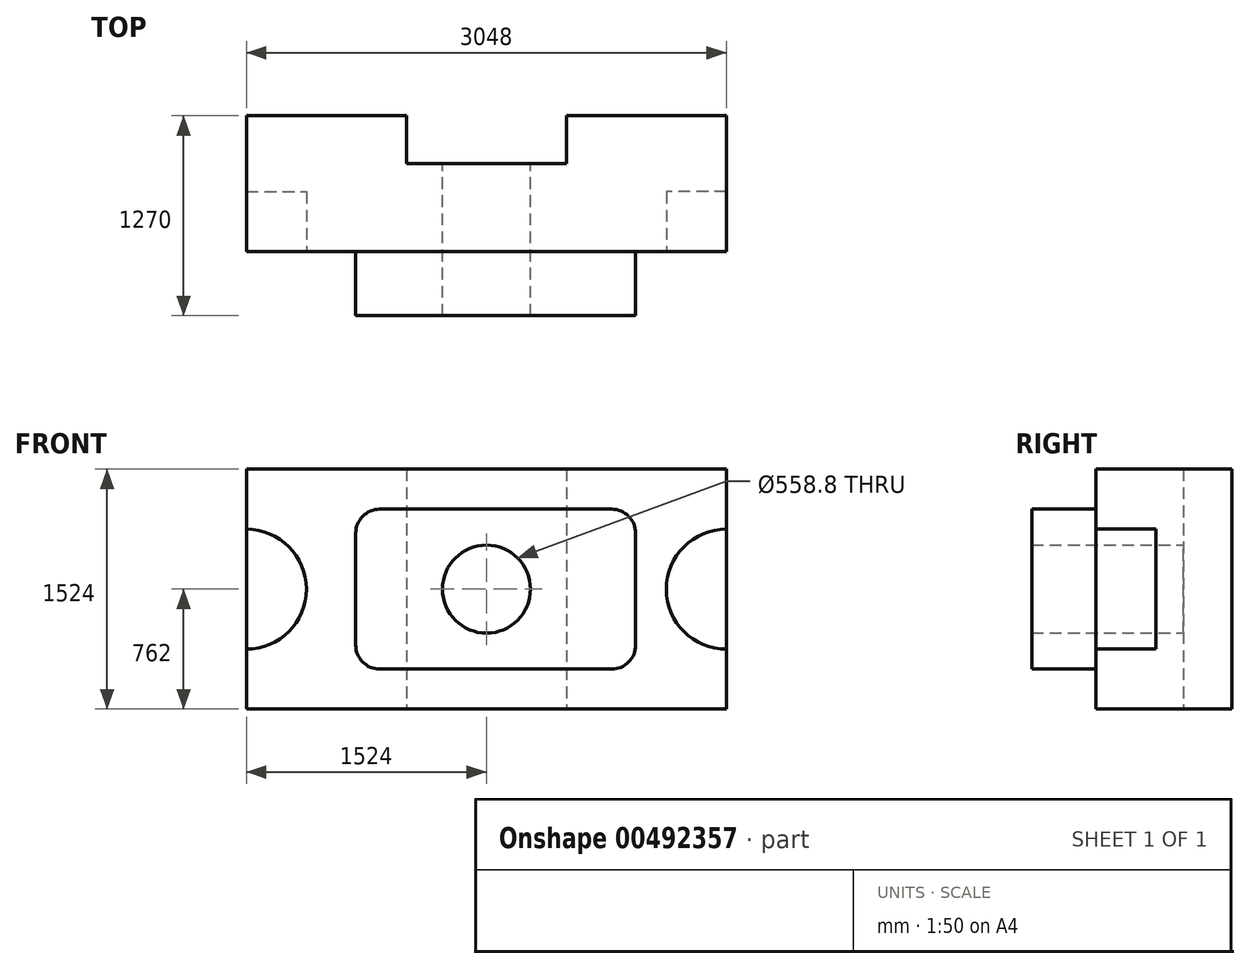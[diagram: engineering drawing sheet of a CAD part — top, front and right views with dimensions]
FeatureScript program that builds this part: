
annotation { "Feature Type Name" : "Feature", "Feature Type Description" : "" }
export const myFeature = defineFeature(function(context is Context, id is Id, definition is map)
    precondition{}
    {
        {
            var Q0;
            Q0=qCreatedBy(makeId("Front.planeOp"),FACE);
            var sketch = newSketch(context, id + "F0", { "sketchPlane" : qUnion([Q0])});
            skLineSegment(sketch, "E0.bottom", {"start": v(1524, -762) * mm, "end": v(-1524, -762) * mm});
            skLineSegment(sketch, "E0.top", {"start": v(1524, 762) * mm, "end": v(-1524, 762) * mm});
            skLineSegment(sketch, "E0.left", {"start": v(1524, -762) * mm, "end": v(1524, 762) * mm});
            skLineSegment(sketch, "E0.right", {"start": v(-1524, -762) * mm, "end": v(-1524, 762) * mm});
            skPoint(sketch, "E0.middle", {"position": v(0, 0) * mm});
            skSolve(sketch);
        }
        {
            var Q0;
            Q0=makeQuery(id+"F0.imprint","IMPRINT",FACE,{"disambiguationData":[TD([[makeQuery(id+"F0.imprint","IMPRINT",EDGE,{"derivedFrom":sQuery(id+"F0.wireOp",EDGE,"E0.bottom")}),-1.0]])]});
            extrude(context, id + "F1", {"entities" : qUnion([Q0]), "depth" : 863.6 * mm});
        }
        {
            var Q0;
            Q0=makeQuery(id+"F1.opExtrude","CAP_FACE",FACE,{"disambiguationData":[OSD([sQuery(id+"F0.wireOp",EDGE,"E0.bottom"),sQuery(id+"F0.wireOp",EDGE,"E0.top"),sQuery(id+"F0.wireOp",EDGE,"E0.left"),sQuery(id+"F0.wireOp",EDGE,"E0.right")])],"isStart":false});
            var sketch = newSketch(context, id + "F2", { "sketchPlane" : qUnion([Q0])});
            skArc(sketch, "E1", {"start": v(-1524, -381) * mm, "mid": v(-1143, 0) * mm, "end": v(-1524, 381) * mm});
            skArc(sketch, "E2", {"start": v(1524, 381) * mm, "mid": v(1143, 0) * mm, "end": v(1524, -381) * mm});
            skLineSegment(sketch, "E3", {"start": v(-1524, 381) * mm, "end": v(-1524, -381) * mm});
            skLineSegment(sketch, "E4", {"start": v(1524, 381) * mm, "end": v(1524, -381) * mm});
            skSolve(sketch);
        }
        {
            var Q0;
            Q0=makeQuery(id+"F2.imprint","IMPRINT",FACE,{"disambiguationData":[TD([[makeQuery(id+"F2.imprint","IMPRINT",EDGE,{"derivedFrom":sQuery(id+"F2.wireOp",EDGE,"E1")}),1.0]])]});
            var Q1;
            Q1=makeQuery(id+"F2.imprint","IMPRINT",FACE,{"disambiguationData":[TD([[makeQuery(id+"F2.imprint","IMPRINT",EDGE,{"derivedFrom":sQuery(id+"F2.wireOp",EDGE,"E2")}),1.0]])]});
            extrude(context, id + "F3", {"entities" : qUnion([Q0, Q1]), "operationType" : NewBodyOperationType.REMOVE, "oppositeDirection" : true, "depth" : 381 * mm});
        }
        {
            var Q0;
            Q0=makeQuery(id+"F1.opExtrude","SWEPT_FACE",FACE,{"disambiguationData":[OSD([sQuery(id+"F0.wireOp",EDGE,"E0.bottom")])]});
            var sketch = newSketch(context, id + "F4", { "sketchPlane" : qUnion([Q0])});
            skLineSegment(sketch, "E5.top", {"start": v(508, 304.8) * mm, "end": v(-508, 304.8) * mm});
            skLineSegment(sketch, "E5.left", {"start": v(508, 0) * mm, "end": v(508, 304.8) * mm});
            skLineSegment(sketch, "E5.right", {"start": v(-508, 0) * mm, "end": v(-508, 304.8) * mm});
            skPoint(sketch, "E5.middle", {"position": v(0, 0) * mm});
            skLineSegment(sketch, "E6", {"start": v(-508, 0) * mm, "end": v(508, 0) * mm});
            skPoint(sketch, "E5.bottom.end.orphan", {"position": v(-508, -304.8) * mm});
            skPoint(sketch, "E7.orphan", {"position": v(508, -304.8) * mm});
            skSolve(sketch);
        }
        {
            var Q0;
            Q0=makeQuery(id+"F4.imprint","IMPRINT",FACE,{"disambiguationData":[TD([[makeQuery(id+"F4.imprint","IMPRINT",EDGE,{"derivedFrom":sQuery(id+"F4.wireOp",EDGE,"E5.top")}),1.0]])]});
            extrude(context, id + "F5", {"entities" : qUnion([Q0]), "operationType" : NewBodyOperationType.REMOVE, "endBound" : BoundingType.THROUGH_ALL, "oppositeDirection" : true, "depth" : 25.4 * mm});
        }
        {
            var Q0;
            Q0=makeQuery(id+"F1.opExtrude","CAP_FACE",FACE,{"disambiguationData":[OSD([sQuery(id+"F0.wireOp",EDGE,"E0.bottom"),sQuery(id+"F0.wireOp",EDGE,"E0.top"),sQuery(id+"F0.wireOp",EDGE,"E0.left"),sQuery(id+"F0.wireOp",EDGE,"E0.right")])],"isStart":false});
            var sketch = newSketch(context, id + "F6", { "sketchPlane" : qUnion([Q0])});
            skLineSegment(sketch, "E8.bottom", {"start": v(795.49, 508) * mm, "end": v(-677.71, 508) * mm});
            skLineSegment(sketch, "E8.top", {"start": v(795.49, -508) * mm, "end": v(-677.71, -508) * mm});
            skLineSegment(sketch, "E8.left", {"start": v(947.89, 355.6) * mm, "end": v(947.89, -355.6) * mm});
            skLineSegment(sketch, "E8.right", {"start": v(-830.11, 355.6) * mm, "end": v(-830.11, -355.6) * mm});
            skPoint(sketch, "E8.middle", {"position": v(58.89, 0) * mm});
            skPoint(sketch, "E9.visualSharp", {"position": v(-830.11, 508) * mm});
            skArc(sketch, "E9.filletArc", {"start": v(-677.71, 508) * mm, "mid": v(-785.48, 463.36) * mm, "end": v(-830.11, 355.6) * mm});
            skPoint(sketch, "E10.visualSharp", {"position": v(947.89, 508) * mm});
            skArc(sketch, "E10.filletArc", {"start": v(947.89, 355.6) * mm, "mid": v(903.25, 463.36) * mm, "end": v(795.49, 508) * mm});
            skPoint(sketch, "E11.visualSharp", {"position": v(947.89, -508) * mm});
            skArc(sketch, "E11.filletArc", {"start": v(795.49, -508) * mm, "mid": v(903.25, -463.36) * mm, "end": v(947.89, -355.6) * mm});
            skPoint(sketch, "E12.visualSharp", {"position": v(-830.11, -508) * mm});
            skArc(sketch, "E12.filletArc", {"start": v(-830.11, -355.6) * mm, "mid": v(-785.48, -463.36) * mm, "end": v(-677.71, -508) * mm});
            skSolve(sketch);
        }
        {
            var Q0;
            Q0=makeQuery(id+"F6.imprint","IMPRINT",FACE,{"disambiguationData":[TD([[makeQuery(id+"F6.imprint","IMPRINT",EDGE,{"derivedFrom":sQuery(id+"F6.wireOp",EDGE,"E8.bottom")}),1.0]])]});
            extrude(context, id + "F7", {"entities" : qUnion([Q0]), "operationType" : NewBodyOperationType.ADD, "depth" : 406.4 * mm});
        }
        {
            var Q0;
            Q0=makeQuery(id+"F1.opExtrude","CAP_FACE",FACE,{"disambiguationData":[OSD([sQuery(id+"F0.wireOp",EDGE,"E0.bottom"),sQuery(id+"F0.wireOp",EDGE,"E0.top"),sQuery(id+"F0.wireOp",EDGE,"E0.left"),sQuery(id+"F0.wireOp",EDGE,"E0.right")])],"isStart":false});
            var sketch = newSketch(context, id + "F8", { "sketchPlane" : qUnion([Q0])});
            skCircle(sketch, "E13", {"center": v(0, 0) * mm, "radius": 279.4 * mm});
            skSolve(sketch);
        }
        {
            var Q0;
            Q0 = qSketchRegion(id + "F8", true);
            extrude(context, id + "F9", {"entities" : qUnion([Q0]), "operationType" : NewBodyOperationType.REMOVE, "endBound" : BoundingType.THROUGH_ALL, "depth" : 25.4 * mm});
        }
        {
            var Q0;
            Q0=makeQuery(id+"F9.boolean.opBoolean","COPY",FACE,{"derivedFrom":makeQuery(id+"F9.opExtrude","CAP_FACE",FACE,{"disambiguationData":[OSD([sQuery(id+"F8.wireOp",EDGE,"E13")])],"isStart":true})});
            extrude(context, id + "F10", {"entities" : qUnion([Q0]), "operationType" : NewBodyOperationType.REMOVE, "endBound" : BoundingType.THROUGH_ALL, "oppositeDirection" : true, "depth" : 25.4 * mm});
        }
    });
